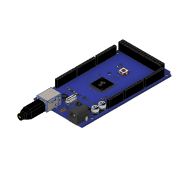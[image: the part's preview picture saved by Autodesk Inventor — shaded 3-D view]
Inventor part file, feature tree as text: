
AUTODESK INVENTOR PART (.ipt)
format: ipt  version: 2022 (Build 260153000, 153)  size: 18,690,048 bytes
history: native  units: mm
features: other x132, sketch x7, extrude x4, plane x2, loft x2, projected_geometry x2, boolean_combine x1
ambient origin geometry x8: Origin, YZ Plane, XZ Plane, XY Plane, X Axis, Y Axis, Z Axis, Center Point
bodies: Solid197 (feature_tree), Solid198 (feature_tree)
feature tree (150):
  extrude  "Extrusion1"  Depth=15.0mm TaperAngle=0.0deg
  extrude  "Extrusion2"  Depth=4.0mm
  plane  "Work Plane1"
  loft  "Loft1"
  plane  "Work Plane2"
  loft  "Loft2"
  extrude  "Extrusion3"  Depth=3.0mm
  boolean_combine  "Combine1"
  extrude  "Extrusion4"  TaperAngle=0.0deg  [1 undecoded]
  sketch  "Sketch7"  dims[d17=0.0mm d18=90.0deg d19=2.0mm d20=0.0mm d21=15.0mm d22=0.0mm]
  other  "Sólido66"
  other  "Sólido68"
  other  "Sólido69"
  other  "Sólido70"
  other  "Sólido71"
  other  "Sólido72"
  other  "Sólido73"
  other  "Sólido74"
  other  "Sólido75"
  other  "Sólido77"
  other  "Sólido78"
  other  "Sólido143"
  other  "Sólido144"
  other  "Sólido145"
  other  "Sólido146"
  other  "Sólido147"
  other  "Sólido148"
  other  "Sólido149"
  other  "Sólido150"
  other  "Sólido151"
  other  "Sólido152"
  other  "Sólido153"
  other  "Sólido154"
  other  "Sólido155"
  other  "Sólido156"
  other  "Sólido157"
  other  "Sólido158"
  other  "Sólido159"
  other  "Sólido160"
  other  "Sólido161"
  other  "Sólido162"
  other  "Sólido163"
  other  "Sólido164"
  other  "Sólido165"
  other  "Sólido166"
  other  "Sólido167"
  other  "Sólido168"
  other  "Sólido169"
  other  "Sólido170"
  other  "Sólido171"
  other  "Sólido172"
  other  "Sólido173"
  other  "Sólido174"
  other  "Sólido175"
  other  "Sólido176"
  other  "Sólido177"
  other  "Sólido178"
  other  "Sólido179"
  other  "Sólido180"
  other  "Sólido181"
  other  "Sólido182"
  other  "Sólido183"
  other  "Sólido184"
  other  "Sólido185"
  other  "Sólido186"
  other  "Sólido187"
  other  "Sólido188"
  other  "Sólido189"
  other  "Sólido190"
  other  "Sólido191"
  other  "Sólido192"
  other  "Sólido193"
  other  "Sólido194"
  other  "Sólido195"
  other  "Sólido196"
  sketch  "Sketch1"  dims[d0=1.0mm d1=0.0mm d2=15.0mm d3=0.0mm]
  sketch  "Sketch2"  dims[d4=4.0mm d5=4.0mm]
  sketch  "Sketch3"  dims[d6=6.0mm d7=6.0mm]
  other  "Edges1"
  sketch  "Sketch4"  dims[d8=0.0mm d9=90.0deg d10=0.0mm d11=90.0deg]
  other  "Edges2"
  sketch  "Sketch5"  dims[d12=2.0mm d13=3.0mm]
  projected_geometry  "Projected Loop1"
  sketch  "Sketch6"  dims[d14=3.0mm d15=0.0mm d16=90.0deg]
  projected_geometry  "Projected Loop2"
  other  "Sup2:65"
  other  "Sup2:67"
  other  "Sup2:68"
  other  "Sup2:69"
  other  "Sup2:70"
  other  "Sup2:71"
  other  "Sup2:72"
  other  "Sup2:73"
  other  "Sup2:74"
  other  "Sup2:76"
  other  "Sup2:77"
  other  "Sup2:142"
  other  "Sup3"
  other  "Sup3:1"
  other  "Sup3:2"
  other  "Sup3:3"
  other  "Sup3:4"
  other  "Sup3:5"
  other  "Sup3:6"
  other  "Sup3:7"
  other  "Sup3:8"
  other  "Sup3:9"
  other  "Sup3:10"
  other  "Sup3:11"
  other  "Sup3:12"
  other  "Sup3:13"
  other  "Sup3:14"
  other  "Sup3:15"
  other  "Sup3:16"
  other  "Sup3:17"
  other  "Sup3:18"
  other  "Sup3:19"
  other  "Sup3:20"
  other  "Sup3:21"
  other  "Sup3:22"
  other  "Sup3:23"
  other  "Sup3:24"
  other  "Sup3:25"
  other  "Sup3:26"
  other  "Sup3:27"
  other  "Sup3:28"
  other  "Sup3:29"
  other  "Sup3:30"
  other  "Sup3:31"
  other  "Sup3:32"
  other  "Sup3:33"
  other  "Sup3:34"
  other  "Sup3:35"
  other  "Sup3:36"
  other  "Sup3:37"
  other  "Sup3:38"
  other  "Sup3:39"
  other  "Sup3:40"
  other  "Sup3:41"
  other  "Sup3:42"
  other  "Sup3:43"
  other  "Sup4"
  other  "Sup4:1"
  other  "Sup4:2"
  other  "Sup4:3"
  other  "Sup4:4"
  other  "Sup4:5"
  other  "Sup4:6"
  other  "Sólido1:1"
  other  "Sólido1:2"
note: 1 required parameter value undecoded (feature->parameter linkage not recoverable at this tier; creation-order binding heuristic only, values carry confidence <= 0.55)
